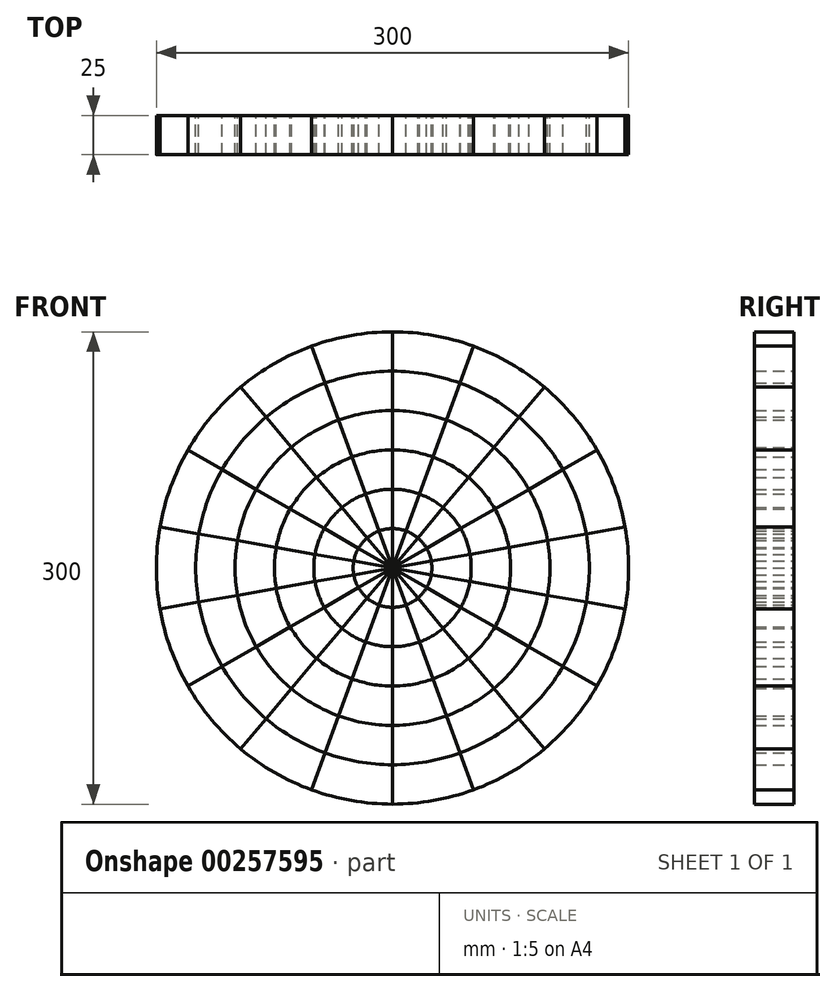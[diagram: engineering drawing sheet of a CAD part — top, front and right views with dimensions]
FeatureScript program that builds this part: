
annotation { "Feature Type Name" : "Feature", "Feature Type Description" : "" }
export const myFeature = defineFeature(function(context is Context, id is Id, definition is map)
    precondition{}
    {
        {
            var Q0;
            Q0=qCreatedBy(makeId("Front.planeOp"),FACE);
            var sketch = newSketch(context, id + "F0", { "sketchPlane" : qUnion([Q0])});
            skCircle(sketch, "E0", {"center": v(0, 0) * mm, "radius": 150 * mm});
            skLineSegment(sketch, "E1", {"start": v(0, 0) * mm, "end": v(0, 150) * mm});
            skLineSegment(sketch, "E2", {"start": v(0, 0) * mm, "end": v(-51.3, 140.95) * mm});
            skCircle(sketch, "E3", {"center": v(0, 0) * mm, "radius": 50 * mm});
            skCircle(sketch, "E4", {"center": v(0, 0) * mm, "radius": 100 * mm});
            skCircle(sketch, "E5", {"center": v(0, 0) * mm, "radius": 25 * mm});
            skCircle(sketch, "E6", {"center": v(0, 0) * mm, "radius": 75 * mm});
            skCircle(sketch, "E7", {"center": v(0, 0) * mm, "radius": 125 * mm});
            skSolve(sketch);
        }
        {
            var Q0;
            {var subQ0=sQuery(id+"F0.wireOp",EDGE,"E1");var subQ1=sQuery(id+"F0.wireOp",EDGE,"E0");var subQ2=makeQuery(id+"F0.imprint","INTERSECT",VERTEX,{"derivedFrom":[subQ1,subQ0]});Q0=makeQuery(id+"F0.imprint","IMPRINT",FACE,{"disambiguationData":[TD([[makeQuery(id+"F0.imprint","IMPRINT",EDGE,{"disambiguationData":[TD([[subQ2,-1.0]])],"derivedFrom":subQ1}),1.0]])]});}
            var Q1;
            {var subQ0=sQuery(id+"F0.wireOp",EDGE,"E6");var subQ1=sQuery(id+"F0.wireOp",EDGE,"E1");var subQ2=makeQuery(id+"F0.imprint","INTERSECT",VERTEX,{"derivedFrom":[subQ1,subQ0]});Q1=makeQuery(id+"F0.imprint","IMPRINT",FACE,{"disambiguationData":[TD([[makeQuery(id+"F0.imprint","IMPRINT",EDGE,{"disambiguationData":[TD([[subQ2,-1.0]])],"derivedFrom":subQ1}),1.0]])]});}
            var Q2;
            {var subQ0=sQuery(id+"F0.wireOp",EDGE,"E5");var subQ1=sQuery(id+"F0.wireOp",EDGE,"E1");var subQ2=makeQuery(id+"F0.imprint","INTERSECT",VERTEX,{"derivedFrom":[subQ1,subQ0]});Q2=makeQuery(id+"F0.imprint","IMPRINT",FACE,{"disambiguationData":[TD([[makeQuery(id+"F0.imprint","IMPRINT",EDGE,{"disambiguationData":[TD([[subQ2,-1.0]])],"derivedFrom":subQ1}),1.0]])]});}
            extrude(context, id + "F1", {"entities" : qUnion([Q0, Q1, Q2]), "depth" : 25 * mm});
        }
        {
            var Q0;
            {var subQ0=sQuery(id+"F0.wireOp",EDGE,"E4");var subQ1=sQuery(id+"F0.wireOp",EDGE,"E1");var subQ2=makeQuery(id+"F0.imprint","INTERSECT",VERTEX,{"derivedFrom":[subQ1,subQ0]});Q0=makeQuery(id+"F0.imprint","IMPRINT",FACE,{"disambiguationData":[TD([[makeQuery(id+"F0.imprint","IMPRINT",EDGE,{"disambiguationData":[TD([[subQ2,-1.0]])],"derivedFrom":subQ1}),1.0]])]});}
            var Q1;
            {var subQ0=sQuery(id+"F0.wireOp",EDGE,"E3");var subQ1=sQuery(id+"F0.wireOp",EDGE,"E1");var subQ2=makeQuery(id+"F0.imprint","INTERSECT",VERTEX,{"derivedFrom":[subQ1,subQ0]});Q1=makeQuery(id+"F0.imprint","IMPRINT",FACE,{"disambiguationData":[TD([[makeQuery(id+"F0.imprint","IMPRINT",EDGE,{"disambiguationData":[TD([[subQ2,-1.0]])],"derivedFrom":subQ1}),1.0]])]});}
            var Q2;
            {var subQ0=sQuery(id+"F0.wireOp",EDGE,"E2");var subQ1=sQuery(id+"F0.wireOp",EDGE,"E1");var subQ2=makeQuery(id+"F0.imprint","INTERSECT",VERTEX,{"derivedFrom":[subQ1,subQ0]});Q2=makeQuery(id+"F0.imprint","IMPRINT",FACE,{"disambiguationData":[TD([[makeQuery(id+"F0.imprint","IMPRINT",EDGE,{"disambiguationData":[TD([[subQ2,-1.0]])],"derivedFrom":subQ1}),1.0]])]});}
            extrude(context, id + "F2", {"entities" : qUnion([Q0, Q1, Q2]), "depth" : 25 * mm});
        }
        {
            var Q0;
            Q0=makeQuery(id+"F1.opExtrude","SWEPT_BODY",BODY,{"disambiguationData":[OSD([sQuery(id+"F0.wireOp",EDGE,"E0"),sQuery(id+"F0.wireOp",EDGE,"E1"),sQuery(id+"F0.wireOp",EDGE,"E2"),sQuery(id+"F0.wireOp",EDGE,"E7")])]});
            var Q1;
            Q1=makeQuery(id+"F2.opExtrude","SWEPT_BODY",BODY,{"disambiguationData":[OSD([sQuery(id+"F0.wireOp",EDGE,"E1"),sQuery(id+"F0.wireOp",EDGE,"E2"),sQuery(id+"F0.wireOp",EDGE,"E4"),sQuery(id+"F0.wireOp",EDGE,"E7")])]});
            var Q2;
            Q2=makeQuery(id+"F1.opExtrude","SWEPT_BODY",BODY,{"disambiguationData":[OSD([sQuery(id+"F0.wireOp",EDGE,"E1"),sQuery(id+"F0.wireOp",EDGE,"E2"),sQuery(id+"F0.wireOp",EDGE,"E4"),sQuery(id+"F0.wireOp",EDGE,"E6")])]});
            var Q3;
            Q3=makeQuery(id+"F2.opExtrude","SWEPT_BODY",BODY,{"disambiguationData":[OSD([sQuery(id+"F0.wireOp",EDGE,"E1"),sQuery(id+"F0.wireOp",EDGE,"E2"),sQuery(id+"F0.wireOp",EDGE,"E3"),sQuery(id+"F0.wireOp",EDGE,"E6")])]});
            var Q4;
            Q4=makeQuery(id+"F1.opExtrude","SWEPT_BODY",BODY,{"disambiguationData":[OSD([sQuery(id+"F0.wireOp",EDGE,"E1"),sQuery(id+"F0.wireOp",EDGE,"E2"),sQuery(id+"F0.wireOp",EDGE,"E3"),sQuery(id+"F0.wireOp",EDGE,"E5")])]});
            var Q5;
            Q5=makeQuery(id+"F2.opExtrude","SWEPT_BODY",BODY,{"disambiguationData":[OSD([sQuery(id+"F0.wireOp",EDGE,"E1"),sQuery(id+"F0.wireOp",EDGE,"E2"),sQuery(id+"F0.wireOp",EDGE,"E5")])]});
            var Q6;
            Q6=makeQuery(id+"F2.opExtrude","SWEPT_EDGE",EDGE,{"disambiguationData":[OSD([sQuery(id+"F0.wireOp",EDGE,"E1"),sQuery(id+"F0.wireOp",EDGE,"E2")])]});
            circularPattern(context, id + "F3", {"entities" : qUnion([Q0, Q1, Q2, Q3, Q4, Q5]), "axis" : qUnion([Q6]), "angle" : 360 * degree, "instanceCount" : 18, "equalSpace" : true});
        }
    });
